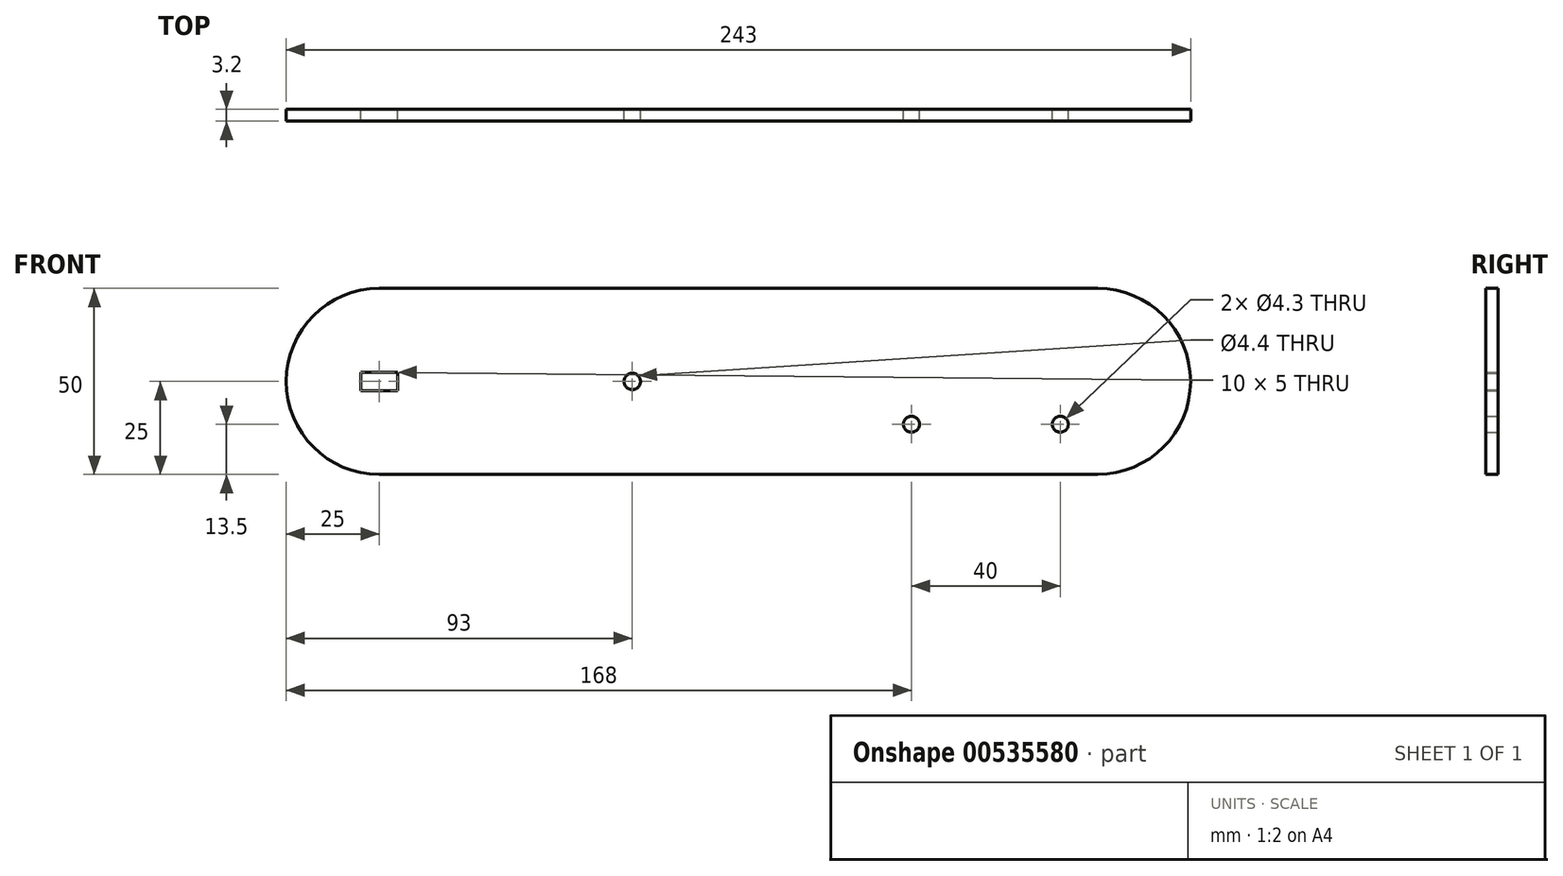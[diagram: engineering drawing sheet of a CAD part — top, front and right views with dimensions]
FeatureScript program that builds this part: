
annotation { "Feature Type Name" : "Feature", "Feature Type Description" : "" }
export const myFeature = defineFeature(function(context is Context, id is Id, definition is map)
    precondition{}
    {
        {
            var Q0;
            Q0=qCreatedBy(makeId("Front.planeOp"),FACE);
            var sketch = newSketch(context, id + "F0", { "sketchPlane" : qUnion([Q0])});
            skCircle(sketch, "E0", {"center": v(-68, 0) * mm, "radius": 25 * mm});
            skCircle(sketch, "E1", {"center": v(125, 0) * mm, "radius": 25 * mm});
            skLineSegment(sketch, "E2", {"start": v(-68, -25) * mm, "end": v(-68, 25) * mm});
            skLineSegment(sketch, "E3", {"start": v(125, 25) * mm, "end": v(125, -25) * mm});
            skLineSegment(sketch, "E4", {"start": v(-68, 25) * mm, "end": v(125, 25) * mm});
            skLineSegment(sketch, "E5", {"start": v(125, -25) * mm, "end": v(-68, -25) * mm});
            skSolve(sketch);
        }
        {
            var Q0;
            Q0 = qSketchRegion(id + "F0", true);
            extrude(context, id + "F1", {"entities" : qUnion([Q0]), "depth" : 3.2 * mm, "offsetDistance" : 25 * mm});
        }
        {
            var Q0;
            Q0=qCreatedBy(makeId("Front.planeOp"),FACE);
            var sketch = newSketch(context, id + "F2", { "sketchPlane" : qUnion([Q0])});
            skCircle(sketch, "E6", {"center": v(0, 0) * mm, "radius": 2.2 * mm});
            skCircle(sketch, "E7", {"center": v(-68, 0) * mm, "radius": 2.5 * mm});
            skLineSegment(sketch, "E8.bottom", {"start": v(-63, 2.5) * mm, "end": v(-73, 2.5) * mm});
            skLineSegment(sketch, "E8.top", {"start": v(-63, -2.5) * mm, "end": v(-73, -2.5) * mm});
            skLineSegment(sketch, "E8.left", {"start": v(-63, 2.5) * mm, "end": v(-63, -2.5) * mm});
            skLineSegment(sketch, "E8.right", {"start": v(-73, 2.5) * mm, "end": v(-73, -2.5) * mm});
            skCircle(sketch, "E9.MirrorC", {"center": v(75, -11.5) * mm, "radius": 2.15 * mm});
            skCircle(sketch, "E10.MirrorC", {"center": v(115, -11.5) * mm, "radius": 2.15 * mm});
            skSolve(sketch);
        }
        {
            var Q0;
            Q0 = qSketchRegion(id + "F2", true);
            extrude(context, id + "F3", {"entities" : qUnion([Q0]), "operationType" : NewBodyOperationType.REMOVE, "depth" : 25 * mm, "offsetDistance" : 25 * mm, "symmetric" : true});
        }
    });
